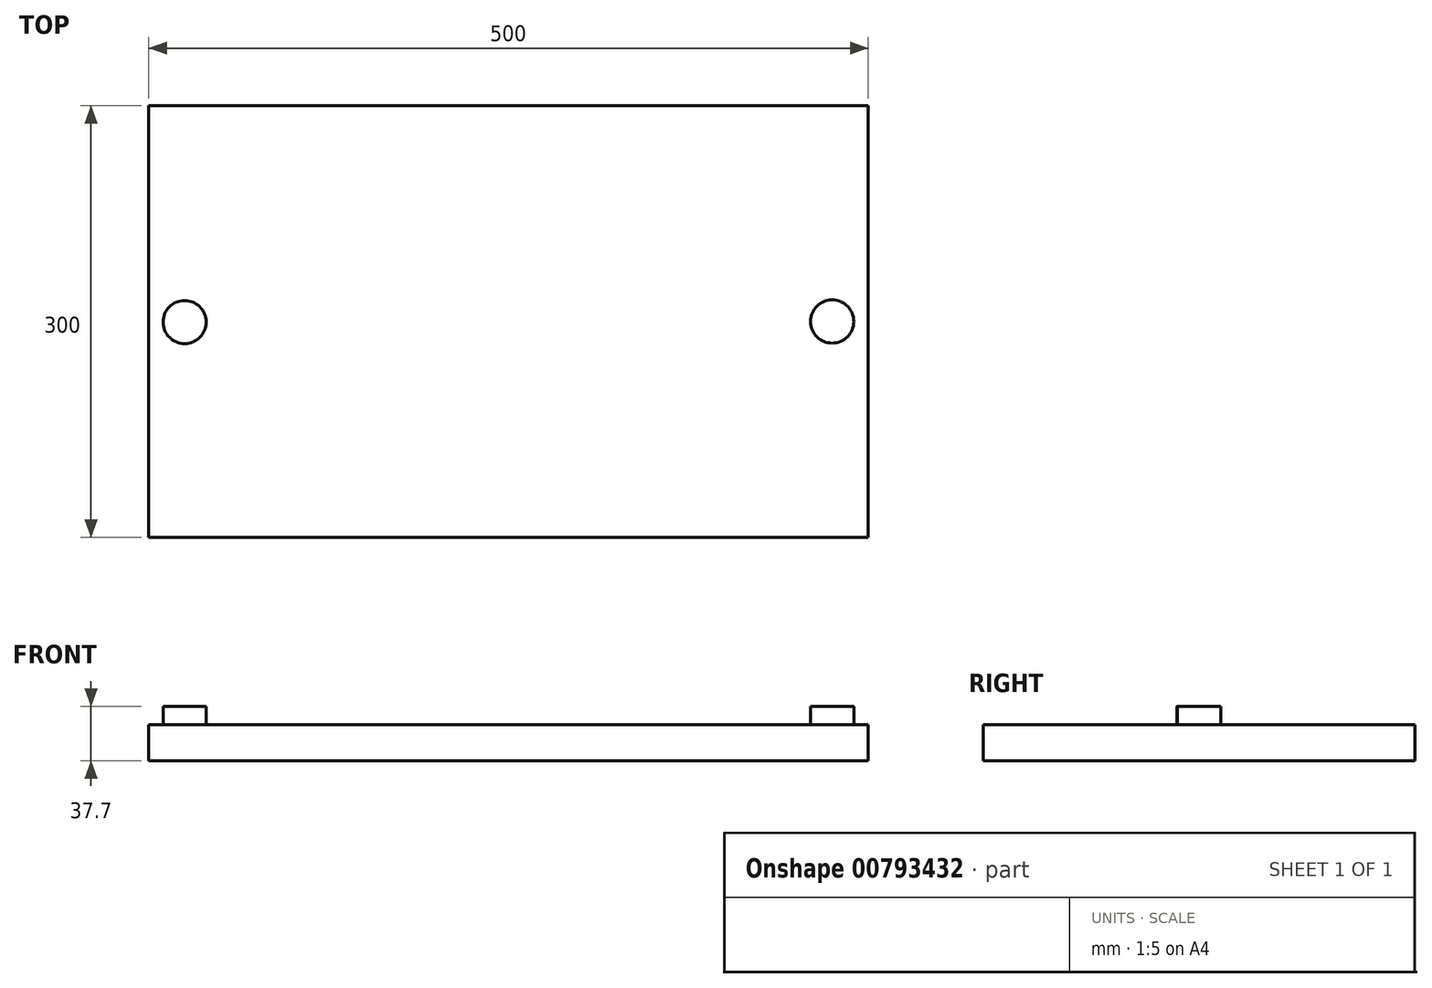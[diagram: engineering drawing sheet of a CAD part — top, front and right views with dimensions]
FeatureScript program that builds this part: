
annotation { "Feature Type Name" : "Feature", "Feature Type Description" : "" }
export const myFeature = defineFeature(function(context is Context, id is Id, definition is map)
    precondition{}
    {
        {
            var Q0;
            Q0=qCreatedBy(makeId("Top.planeOp"),FACE);
            var sketch = newSketch(context, id + "F0", { "sketchPlane" : qUnion([Q0])});
            skLineSegment(sketch, "E0.bottom", {"start": v(0, 0) * mm, "end": v(500, 0) * mm});
            skLineSegment(sketch, "E0.top", {"start": v(0, -300) * mm, "end": v(500, -300) * mm});
            skLineSegment(sketch, "E0.left", {"start": v(0, 0) * mm, "end": v(0, -300) * mm});
            skLineSegment(sketch, "E0.right", {"start": v(500, 0) * mm, "end": v(500, -300) * mm});
            skSolve(sketch);
        }
        {
            var Q0;
            Q0=makeQuery(id+"F0.imprint","IMPRINT",FACE,{"disambiguationData":[TD([[makeQuery(id+"F0.imprint","IMPRINT",EDGE,{"derivedFrom":sQuery(id+"F0.wireOp",EDGE,"E0.bottom")}),-1.0]])]});
            extrude(context, id + "F1", {"entities" : qUnion([Q0]), "depth" : 25 * mm, "offsetDistance" : 25.4 * mm});
        }
        {
            var Q0;
            Q0=makeQuery(id+"F1.opExtrude","CAP_FACE",FACE,{"disambiguationData":[OSD([sQuery(id+"F0.wireOp",EDGE,"E0.bottom"),sQuery(id+"F0.wireOp",EDGE,"E0.top"),sQuery(id+"F0.wireOp",EDGE,"E0.left"),sQuery(id+"F0.wireOp",EDGE,"E0.right")])],"isStart":false});
            var sketch = newSketch(context, id + "F2", { "sketchPlane" : qUnion([Q0])});
            skCircle(sketch, "E1", {"center": v(25, -150.43) * mm, "radius": 15 * mm});
            skCircle(sketch, "E2", {"center": v(475, -150) * mm, "radius": 15 * mm});
            skSolve(sketch);
        }
        {
            var Q0;
            Q0=makeQuery(id+"F2.imprint","IMPRINT",FACE,{"disambiguationData":[TD([[makeQuery(id+"F2.imprint","IMPRINT",EDGE,{"derivedFrom":sQuery(id+"F2.wireOp",EDGE,"E1")}),1.0]])]});
            var Q1;
            Q1=makeQuery(id+"F2.imprint","IMPRINT",FACE,{"disambiguationData":[TD([[makeQuery(id+"F2.imprint","IMPRINT",EDGE,{"derivedFrom":sQuery(id+"F2.wireOp",EDGE,"E2")}),1.0]])]});
            extrude(context, id + "F3", {"entities" : qUnion([Q0, Q1]), "operationType" : NewBodyOperationType.ADD, "depth" : 12.7 * mm, "offsetDistance" : 25.4 * mm});
        }
    });
